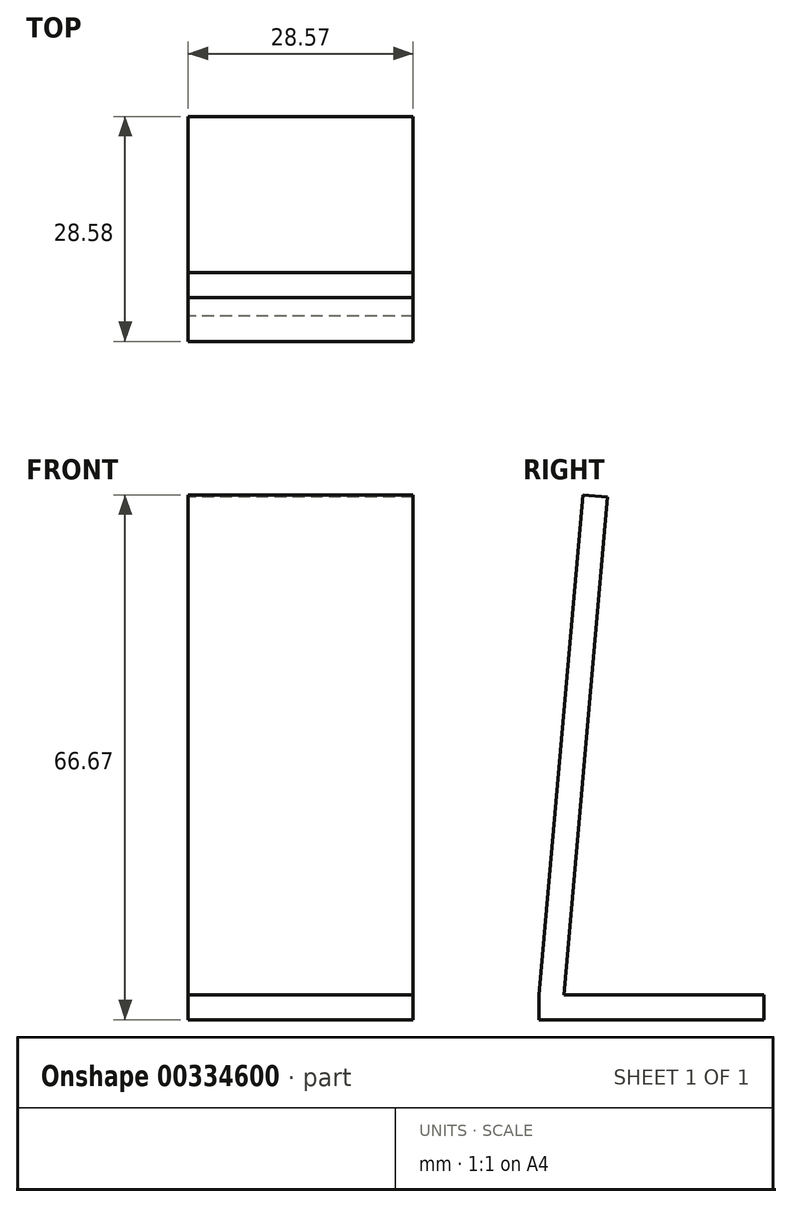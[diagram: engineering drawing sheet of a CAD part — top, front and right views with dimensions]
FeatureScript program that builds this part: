
annotation { "Feature Type Name" : "Feature", "Feature Type Description" : "" }
export const myFeature = defineFeature(function(context is Context, id is Id, definition is map)
    precondition{}
    {
        {
            var Q0;
            Q0=qCreatedBy(makeId("Right.planeOp"),FACE);
            var sketch = newSketch(context, id + "F0", { "sketchPlane" : qUnion([Q0])});
            skLineSegment(sketch, "E0", {"start": v(-14.29, 0) * mm, "end": v(14.29, 0) * mm});
            skLineSegment(sketch, "E1", {"start": v(14.29, 0) * mm, "end": v(14.29, 3.17) * mm});
            skLineSegment(sketch, "E2", {"start": v(14.29, 3.17) * mm, "end": v(-14.29, 3.17) * mm});
            skLineSegment(sketch, "E3", {"start": v(-14.29, 3.17) * mm, "end": v(-14.29, 0) * mm});
            skLineSegment(sketch, "E4", {"start": v(-5.01, 3.17) * mm, "end": v(-5.01, 66.67) * mm, "construction": true});
            skLineSegment(sketch, "E5", {"start": v(-14.29, 3.18) * mm, "end": v(-8.73, 66.67) * mm});
            skLineSegment(sketch, "E6", {"start": v(-8.73, 66.68) * mm, "end": v(-5.57, 66.4) * mm});
            skLineSegment(sketch, "E7", {"start": v(-5.57, 66.4) * mm, "end": v(-11.1, 3.18) * mm});
            skLineSegment(sketch, "E8", {"start": v(-11.1, 3.17) * mm, "end": v(-14.29, 3.17) * mm});
            skSolve(sketch);
        }
        {
            var Q0;
            Q0=qSketchRegion(id+"F0",true);
            extrude(context, id + "F1", {"entities" : qUnion([Q0]), "depth" : 28.57 * mm});
        }
    });
